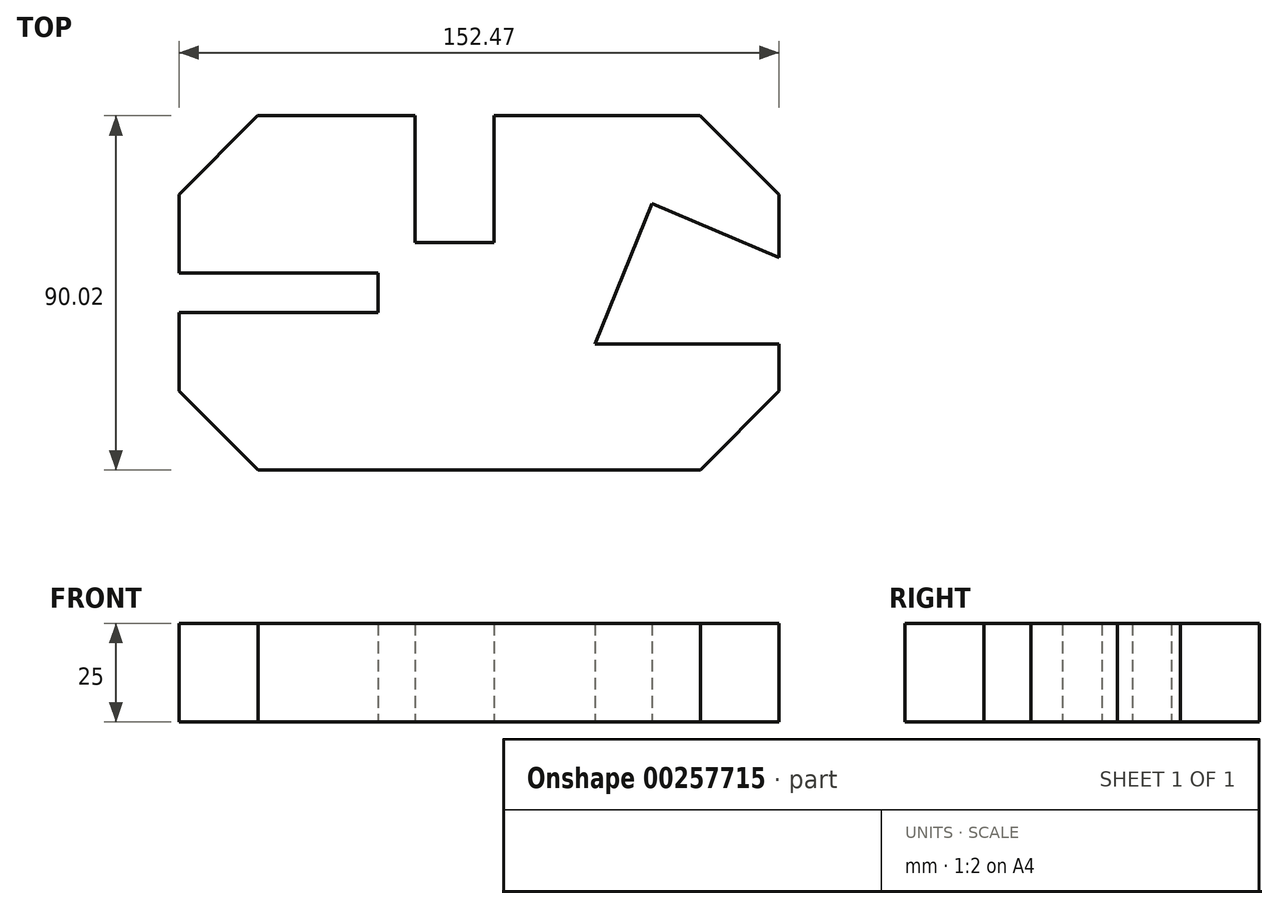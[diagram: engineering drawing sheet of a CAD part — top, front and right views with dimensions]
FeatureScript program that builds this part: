
annotation { "Feature Type Name" : "Feature", "Feature Type Description" : "" }
export const myFeature = defineFeature(function(context is Context, id is Id, definition is map)
    precondition{}
    {
        {
            var Q0;
            Q0=qCreatedBy(makeId("Top.planeOp"),FACE);
            var sketch = newSketch(context, id + "F0", { "sketchPlane" : qUnion([Q0])});
            skLineSegment(sketch, "E0", {"start": v(-48.1, -33.65) * mm, "end": v(64.3, -33.65) * mm});
            skLineSegment(sketch, "E1", {"start": v(-48.1, -33.65) * mm, "end": v(-68.12, -13.64) * mm});
            skLineSegment(sketch, "E2", {"start": v(64.3, -33.65) * mm, "end": v(84.3, -13.64) * mm});
            skLineSegment(sketch, "E3", {"start": v(-68.12, -13.64) * mm, "end": v(-68.12, 6.36) * mm});
            skLineSegment(sketch, "E4", {"start": v(-68.12, 6.36) * mm, "end": v(-17.62, 6.36) * mm});
            skLineSegment(sketch, "E5", {"start": v(-17.62, 6.36) * mm, "end": v(-17.62, 16.36) * mm});
            skLineSegment(sketch, "E6", {"start": v(-17.62, 16.36) * mm, "end": v(-68.17, 16.36) * mm});
            skLineSegment(sketch, "E7", {"start": v(-68.17, 16.36) * mm, "end": v(-68.17, 36.36) * mm});
            skLineSegment(sketch, "E8", {"start": v(-68.17, 36.36) * mm, "end": v(-48.16, 56.37) * mm});
            skLineSegment(sketch, "E9", {"start": v(-48.16, 56.37) * mm, "end": v(-8.16, 56.37) * mm});
            skLineSegment(sketch, "E10", {"start": v(-8.16, 56.37) * mm, "end": v(-8.16, 24.07) * mm});
            skLineSegment(sketch, "E11", {"start": v(-8.16, 24.07) * mm, "end": v(11.84, 24.07) * mm});
            skLineSegment(sketch, "E12", {"start": v(11.84, 24.07) * mm, "end": v(11.84, 56.37) * mm});
            skLineSegment(sketch, "E13", {"start": v(11.84, 56.37) * mm, "end": v(64.24, 56.37) * mm});
            skLineSegment(sketch, "E14", {"start": v(64.24, 56.37) * mm, "end": v(84.25, 36.36) * mm});
            skLineSegment(sketch, "E15", {"start": v(84.25, 36.36) * mm, "end": v(84.25, 20.36) * mm});
            skLineSegment(sketch, "E16", {"start": v(84.25, 20.36) * mm, "end": v(51.98, 34.05) * mm});
            skLineSegment(sketch, "E17", {"start": v(51.98, 34.05) * mm, "end": v(37.56, -1.64) * mm});
            skLineSegment(sketch, "E18", {"start": v(37.56, -1.64) * mm, "end": v(82.86, -1.64) * mm});
            skLineSegment(sketch, "E19", {"start": v(84.3, -13.64) * mm, "end": v(84.3, -1.64) * mm});
            skLineSegment(sketch, "E20", {"start": v(84.3, -1.64) * mm, "end": v(37.56, -1.64) * mm});
            skSolve(sketch);
        }
        {
            var Q0;
            Q0 = qSketchRegion(id + "F0", true);
            extrude(context, id + "F1", {"entities" : qUnion([Q0]), "depth" : 25 * mm});
        }
        {
            var Q0;
            Q0 = qSketchRegion(id + "F0", true);
            extrude(context, id + "F2", {"entities" : qUnion([Q0]), "depth" : 25 * mm});
        }
        {
            var Q0;
            Q0 = qSketchRegion(id + "F0", true);
            extrude(context, id + "F3", {"entities" : qUnion([Q0]), "depth" : 25 * mm});
        }
    });
